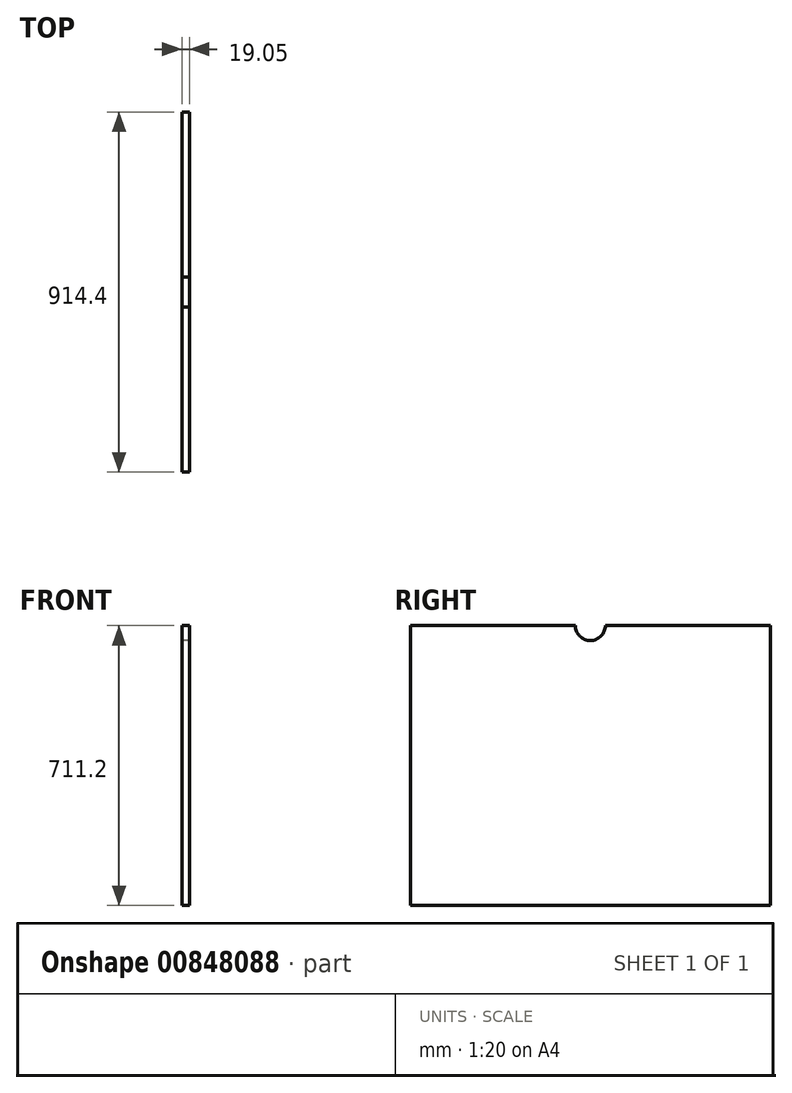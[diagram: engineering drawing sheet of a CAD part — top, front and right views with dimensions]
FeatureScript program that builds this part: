
annotation { "Feature Type Name" : "Feature", "Feature Type Description" : "" }
export const myFeature = defineFeature(function(context is Context, id is Id, definition is map)
    precondition{}
    {
        {
            var Q0;
            Q0=qCreatedBy(makeId("Right.planeOp"),FACE);
            var sketch = newSketch(context, id + "F0", { "sketchPlane" : qUnion([Q0])});
            skLineSegment(sketch, "E0.bottom", {"start": v(457.2, 355.6) * mm, "end": v(-457.2, 355.6) * mm});
            skLineSegment(sketch, "E0.top", {"start": v(457.2, -355.6) * mm, "end": v(-457.2, -355.6) * mm});
            skLineSegment(sketch, "E0.left", {"start": v(457.2, 355.6) * mm, "end": v(457.2, -355.6) * mm});
            skLineSegment(sketch, "E0.right", {"start": v(-457.2, 355.6) * mm, "end": v(-457.2, -355.6) * mm});
            skPoint(sketch, "E0.middle", {"position": v(0, 0) * mm});
            skCircle(sketch, "E1", {"center": v(0, 355.6) * mm, "radius": 38.1 * mm});
            skSolve(sketch);
        }
        {
            var Q0;
            Q0=makeQuery(id+"F0.imprint","IMPRINT",FACE,{"disambiguationData":[TD([[makeQuery(id+"F0.imprint","IMPRINT",EDGE,{"derivedFrom":sQuery(id+"F0.wireOp",EDGE,"E0.top")}),-1.0]])]});
            extrude(context, id + "F1", {"entities" : qUnion([Q0]), "depth" : 19.05 * mm, "offsetDistance" : 25.4 * mm});
        }
    });
